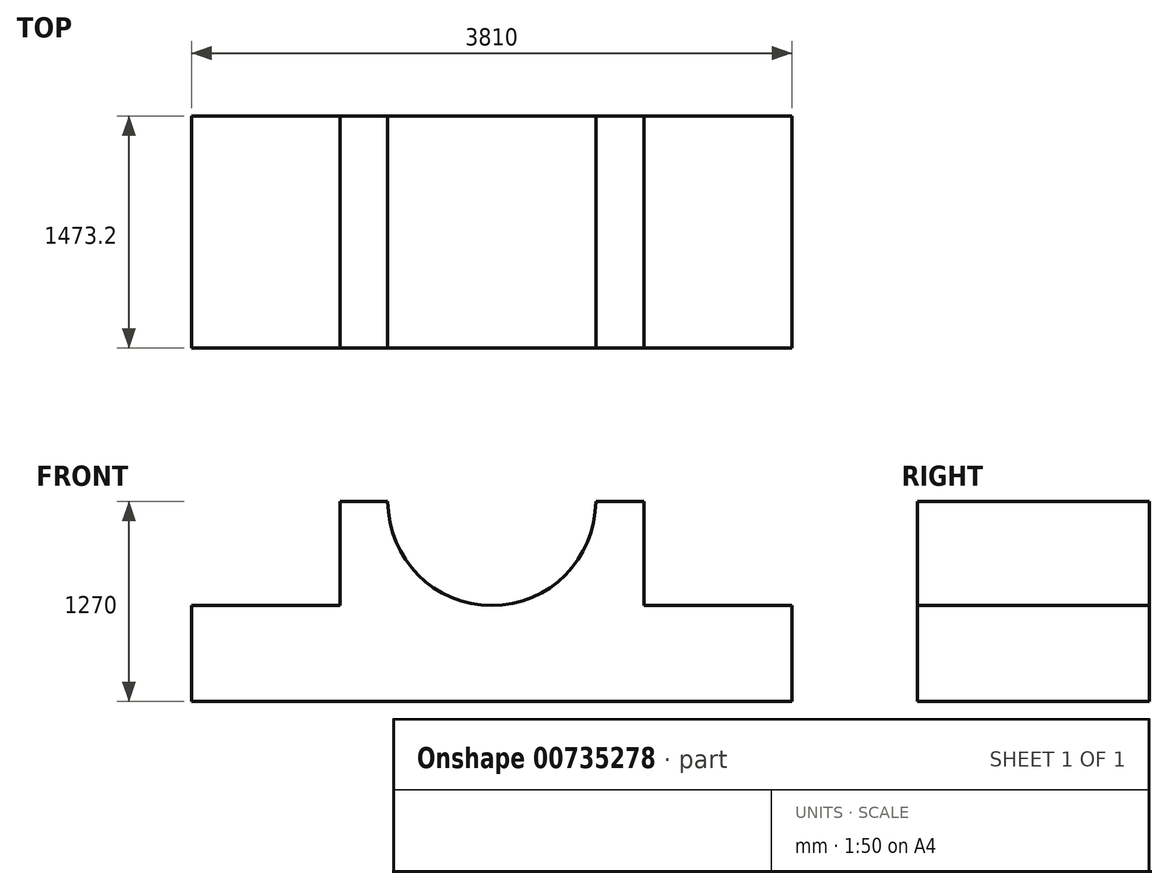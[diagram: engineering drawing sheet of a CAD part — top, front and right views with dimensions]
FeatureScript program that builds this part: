
annotation { "Feature Type Name" : "Feature", "Feature Type Description" : "" }
export const myFeature = defineFeature(function(context is Context, id is Id, definition is map)
    precondition{}
    {
        {
            var Q0;
            Q0=qCreatedBy(makeId("Front.planeOp"),FACE);
            var sketch = newSketch(context, id + "F0", { "sketchPlane" : qUnion([Q0])});
            skLineSegment(sketch, "E0", {"start": v(-98.73, -11.28) * mm, "end": v(3711.27, -11.28) * mm});
            skLineSegment(sketch, "E1", {"start": v(3711.27, -11.28) * mm, "end": v(3711.27, 598.32) * mm});
            skLineSegment(sketch, "E2", {"start": v(-98.73, -11.28) * mm, "end": v(-98.73, 598.32) * mm});
            skLineSegment(sketch, "E3", {"start": v(-98.73, 598.32) * mm, "end": v(841.07, 598.32) * mm});
            skLineSegment(sketch, "E4", {"start": v(3711.27, 598.32) * mm, "end": v(2771.47, 598.32) * mm});
            skLineSegment(sketch, "E5", {"start": v(841.07, 598.32) * mm, "end": v(841.07, 1258.72) * mm});
            skLineSegment(sketch, "E6", {"start": v(2771.47, 598.32) * mm, "end": v(2771.47, 1258.72) * mm});
            skLineSegment(sketch, "E7", {"start": v(841.07, 1258.72) * mm, "end": v(1145.87, 1258.72) * mm});
            skLineSegment(sketch, "E8", {"start": v(1806.27, 598.32) * mm, "end": v(1806.27, 545.03) * mm, "construction": true});
            skArc(sketch, "E9", {"start": v(1145.87, 1258.72) * mm, "mid": v(1806.27, 598.32) * mm, "end": v(2466.67, 1258.72) * mm});
            skLineSegment(sketch, "E10.trimOffspring", {"start": v(2466.67, 1258.72) * mm, "end": v(2771.47, 1258.72) * mm});
            skSolve(sketch);
        }
        {
            var Q0;
            Q0=makeQuery(id+"F0.imprint","IMPRINT",FACE,{"disambiguationData":[TD([[makeQuery(id+"F0.imprint","IMPRINT",EDGE,{"derivedFrom":sQuery(id+"F0.wireOp",EDGE,"E0")}),1.0]])]});
            extrude(context, id + "F1", {"entities" : qUnion([Q0]), "depth" : 1473.2 * mm, "offsetDistance" : 25.4 * mm});
        }
    });
